# Revit family: Basin-Undercounter-American_Standard-Studio-0426.000
name_source: partatom
category: Plumbing Fixtures
revit_build: Autodesk Revit 2014 (Build: 20130308_1515(x64)
units: mm (PartAtom-declared; Revit-internal decimal feet)

## types (3) — shared parameters
ADA Compliant = Yes
Assembly Code = D2010310
Basin Shape = Oval
Bowl Length = 13 1/2"
Bowl Width = 13 1/2"
CW Connection = Yes
CWFU = 1.5
Cold Water Connection Diameter = 1/2"
Cold Water Connection Height = 10 3/4"
Cold Water Connection Radius = 1/4"
Cold Water Connection Width = 4"
Default Elevation = 34"
Description = Studio Carre Undercounter Sink.
HW Connection = Yes
HWFU = 1.5
Height = 6 3/4"
Hot Water Connection Diameter = 1"
Hot Water Connection Height = 10 3/4"
Hot Water Connection Radius = 1/4"
Hot Water Connection Width = 4"
Installation Type = Countertop
Length = 16"
Manufacturer = American Standard
Price = Prices may vary. Please consult Manufacturer Representative for most up-to-date price list.
Product Documentation Link = https://www.americanstandard-us.com
Product Page URL = https://www.americanstandard-us.com
Revised Date = 12/11/2018
Vent Connection = No
WFU = 2
Waste Connection = Yes
Waste Connection Diameter = 1 1/4"
Waste Connection Height = 13"
Waste Connection Radius = 5/8"
Width = 16"

## per-type parameters (varying)
| type | Finish | Material | URL |
| 0426.000.020 | Vitreous China-American Standard-020-White | Vitreous China-American Standard-020-White | http://www.americanstandard.ca |
| 0426.000.021 | Vitreous China-American Standard-021-Bone | Vitreous China-American Standard-021-Bone | http://www.americanstandard.ca |
| 0426.000.222 | Vitreous China-American Standard-222-Linen | Vitreous China-American Standard-222-Linen | https://www.americanstandard-us.com |

note: column(s) folded — value = type name in every type: Model

## geometry (parser evidence)
native form markers: Sweep x1
no freeform markers — native parametric forms only
